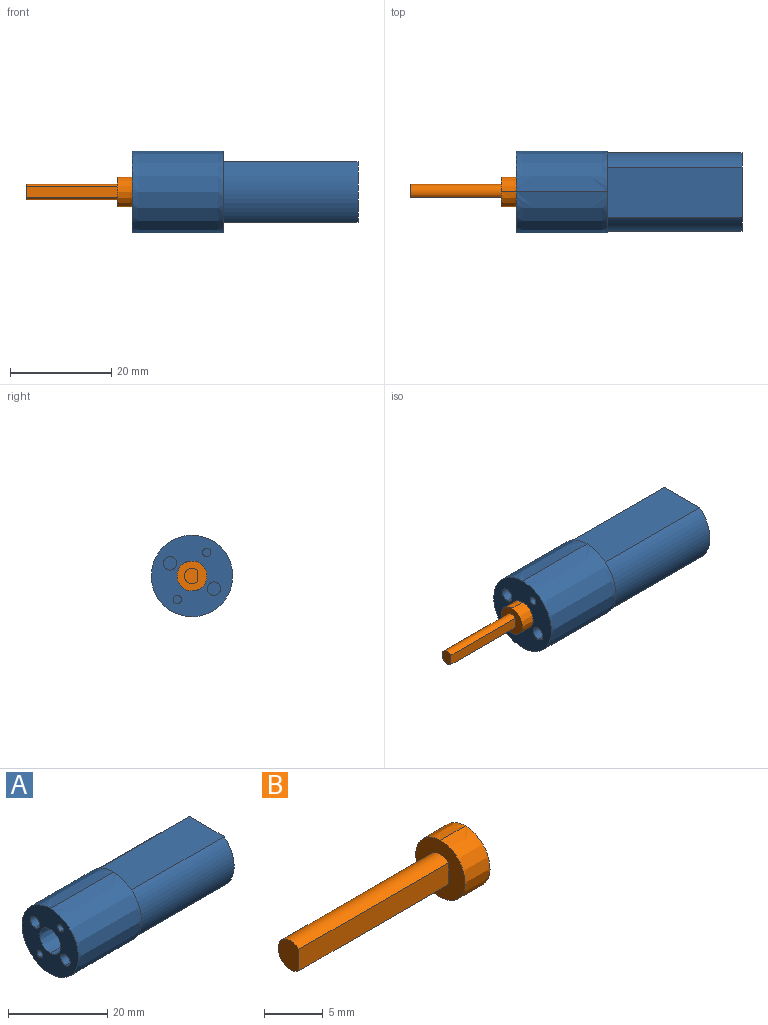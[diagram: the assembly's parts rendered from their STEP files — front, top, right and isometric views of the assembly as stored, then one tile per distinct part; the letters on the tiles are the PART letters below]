
ASSEMBLY  parts=2 mates=1
PART A: 24 faces, bbox 44.6x16.1x16.1 mm
  f0: extruded ~15.57x1.65mm, area 40.4mm2, adj f9,f13,f19
  f1: extruded ~15.57x2.66mm, area 65.1mm2, adj f5,f13,f23
  f2: extruded ~15.57x5.92mm, area 144.8mm2, adj f6,f13,f22
  f3: extruded ~15.57x2.66mm, area 65.1mm2, adj f7,f13,f21
  f4: extruded ~15.57x1.65mm, area 40.4mm2, adj f8,f13,f20
  f5: extruded ~15.57x2.66mm, area 65.1mm2, adj f1,f13,f23
  f6: extruded ~15.57x5.92mm, area 144.8mm2, adj f2,f13,f22
  f7: extruded ~15.57x2.66mm, area 65.1mm2, adj f3,f13,f21
  f8: extruded ~15.57x1.65mm, area 40.4mm2, adj f4,f13,f20
  f9: extruded ~15.57x1.65mm, area 40.4mm2, adj f0,f13,f19
  f10: extruded ~18x16.08mm, area 454.5mm2, adj f11,f12,f13
  f11: extruded ~18x16.08mm, area 454.5mm2, adj f10,f12,f13
  f12: plane 16.08x16.08mm, normal (1,0,0), area 37.1mm2, adj f10,f11,f15,f16,f17,f18
  f13: plane 16.08x16.08mm, normal (-1,0,0), area 160.2mm2, adj f0,f1,f2,f3,f4,f5,f6,f7
  f14: plane 15.55x12.03mm, normal (1,0,0), area 165.9mm2, adj f15,f16,f17,f18
  f15: cylinder r=7.77mm len=26.57mm, axis (1,0,0), area 363.6mm2, adj f12,f14,f16,f18
  f16: plane 26.57x9.88mm, normal (0,0,1), area 262.5mm2, adj f12,f14,f15,f17
  f17: cylinder r=7.77mm len=26.57mm, axis (1,0,0), area 365.5mm2, adj f12,f14,f16,f18
  f18: plane 26.57x9.88mm, normal (0,0,-1), area 262.5mm2, adj f12,f14,f15,f17
  f19: plane 1.65x1.65mm, normal (-1,0,0), area 2.1mm2, adj f0,f9
  f20: plane 1.65x1.65mm, normal (-1,0,0), area 2.1mm2, adj f4,f8
  f21: plane 2.66x2.66mm, normal (-1,0,0), area 5.6mm2, adj f3,f7
  f22: plane 5.92x5.92mm, normal (-1,0,0), area 27.5mm2, adj f2,f6
  f23: plane 2.66x2.66mm, normal (-1,0,0), area 5.6mm2, adj f1,f5
PART B: 10 faces, bbox 21x5.9x5.9 mm
  f0: extruded ~5.92x3mm, area 27.9mm2, adj f1,f2,f3
  f1: extruded ~5.92x3mm, area 27.9mm2, adj f0,f2,f3
  f2: plane 5.92x5.92mm, normal (-1,0,0), area 21.2mm2, adj f0,f1,f7,f8
  f3: plane 5.92x5.92mm, normal (1,0,0), area 21.2mm2, adj f0,f1,f5,f6
  f4: plane 3x2.5mm, normal (1,0,0), area 6.3mm2, adj f5,f6
  f5: plane 2.24x0.01mm, normal (0,-1,0), area 0mm2, adj f3,f4,f6
  f6: cylinder r=1.5mm len=3mm, axis (1,0,0), area 0.1mm2, adj f3,f4,f5
  f7: cylinder r=1.5mm len=17.99mm, axis (1,0,0), area 124.1mm2, adj f2,f8,f9
  f8: plane 17.99x2.24mm, normal (0,-1,0), area 40.3mm2, adj f2,f7,f9
  f9: plane 3x2.5mm, normal (-1,0,0), area 6.3mm2, adj f7,f8
PLACE A t=(6.9,-67.26,-30.38)mm
PLACE B t=(6.9,-67.26,-30.38)mm
MATE fastened B.f6 <-> A.f15  axis (1,0,0) through (-10.86,-67.26,-30.38)mm
